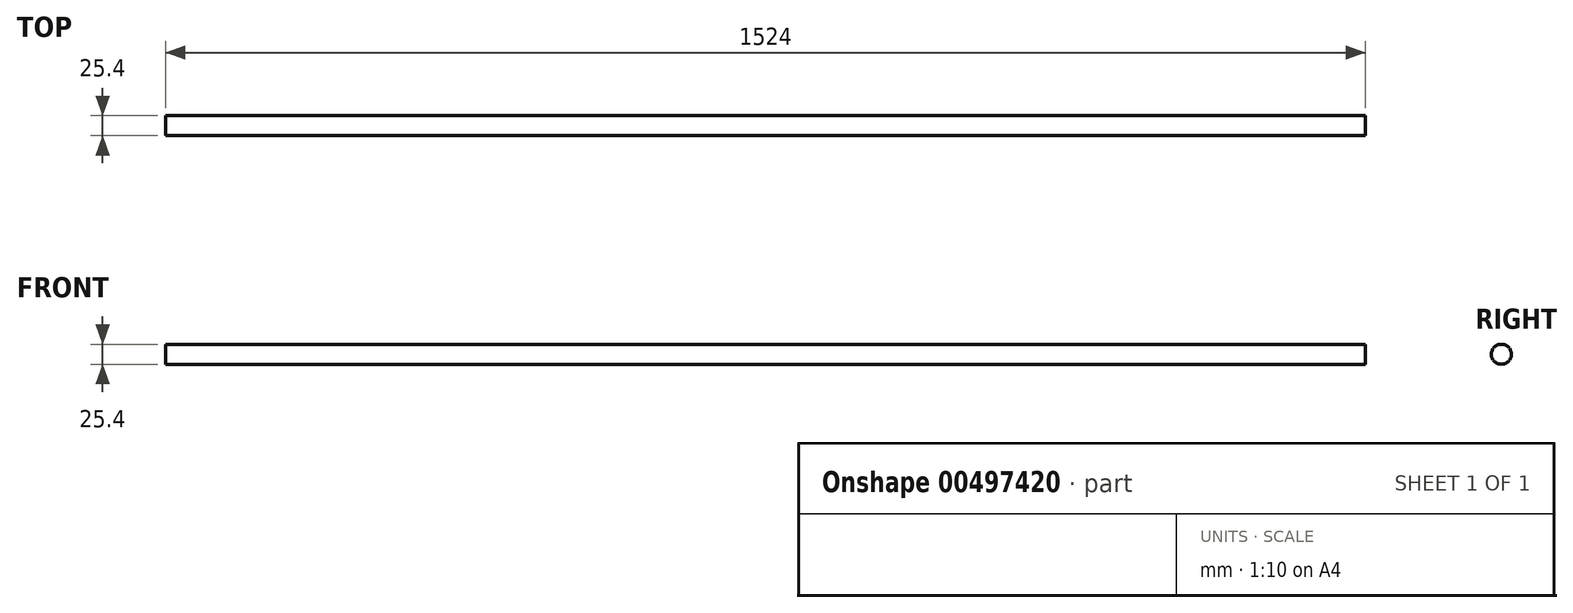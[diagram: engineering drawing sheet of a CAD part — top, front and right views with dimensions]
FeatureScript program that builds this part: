
annotation { "Feature Type Name" : "Feature", "Feature Type Description" : "" }
export const myFeature = defineFeature(function(context is Context, id is Id, definition is map)
    precondition{}
    {
        {
            var Q0;
            Q0=qCreatedBy(makeId("Right.planeOp"),FACE);
            var sketch = newSketch(context, id + "F0", { "sketchPlane" : qUnion([Q0])});
            skCircle(sketch, "E0", {"center": v(3.64, 4.2) * mm, "radius": 12.7 * mm});
            skSolve(sketch);
        }
        {
            var Q0;
            Q0 = qSketchRegion(id + "F0", true);
            extrude(context, id + "F1", {"entities" : qUnion([Q0]), "depth" : 1524 * mm, "offsetDistance" : 25.4 * mm});
        }
    });
